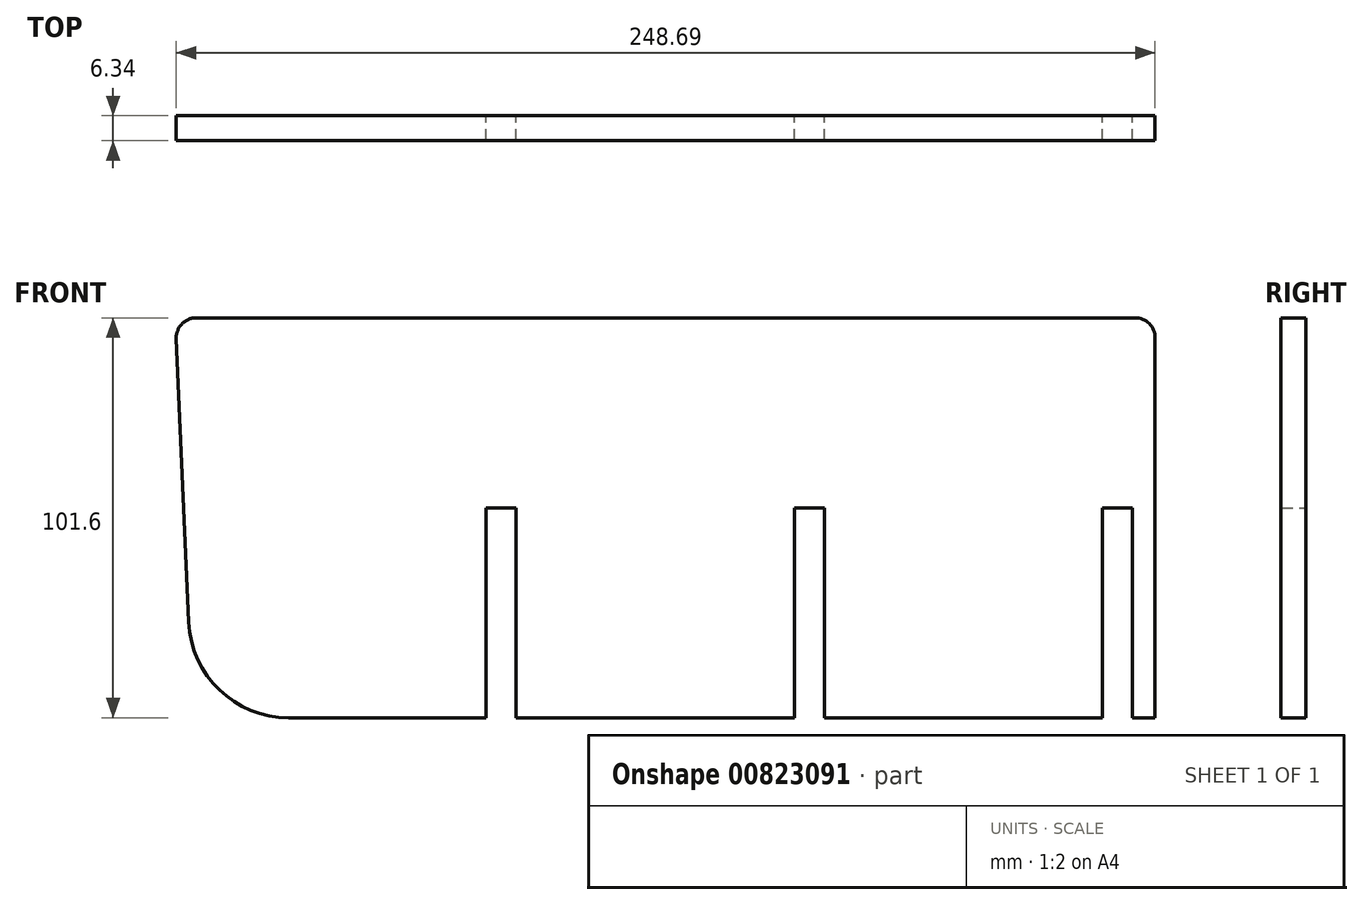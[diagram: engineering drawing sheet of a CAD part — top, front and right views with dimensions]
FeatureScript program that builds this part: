
annotation { "Feature Type Name" : "Feature", "Feature Type Description" : "" }
export const myFeature = defineFeature(function(context is Context, id is Id, definition is map)
    precondition{}
    {
        {
            var Q0;
            Q0=qCreatedBy(makeId("Front.planeOp"),FACE);
            var sketch = newSketch(context, id + "F0", { "sketchPlane" : qUnion([Q0])});
            skLineSegment(sketch, "E0", {"start": v(-126.67, 101.6) * mm, "end": v(-122.24, 0) * mm});
            skLineSegment(sketch, "E1", {"start": v(-122.24, 0) * mm, "end": v(-47.72, 0) * mm});
            skLineSegment(sketch, "E2", {"start": v(122.24, 0) * mm, "end": v(122.24, 101.6) * mm});
            skLineSegment(sketch, "E3", {"start": v(122.24, 101.6) * mm, "end": v(-126.67, 101.6) * mm});
            skLineSegment(sketch, "E4", {"start": v(112.71, 112) * mm, "end": v(112.71, -48.09) * mm, "construction": true});
            skLineSegment(sketch, "E5.top", {"start": v(116.52, 53.34) * mm, "end": v(108.9, 53.34) * mm});
            skLineSegment(sketch, "E5.left", {"start": v(116.52, 0) * mm, "end": v(116.52, 53.34) * mm});
            skLineSegment(sketch, "E5.right", {"start": v(108.9, 0) * mm, "end": v(108.9, 53.34) * mm});
            skLineSegment(sketch, "E6.top", {"start": v(38.2, 53.34) * mm, "end": v(30.59, 53.34) * mm});
            skLineSegment(sketch, "E6.left", {"start": v(38.2, 0) * mm, "end": v(38.2, 53.34) * mm});
            skLineSegment(sketch, "E6.right", {"start": v(30.59, 0) * mm, "end": v(30.59, 53.34) * mm});
            skLineSegment(sketch, "E7", {"start": v(34.4, 109.08) * mm, "end": v(34.4, -45.34) * mm, "construction": true});
            skLineSegment(sketch, "E8.MirrorCS", {"start": v(-47.72, 53.34) * mm, "end": v(-40.1, 53.34) * mm});
            skLineSegment(sketch, "E9.MirrorCS", {"start": v(-47.72, 0) * mm, "end": v(-47.72, 53.34) * mm});
            skLineSegment(sketch, "E10.MirrorCS", {"start": v(-40.1, 0) * mm, "end": v(-40.1, 53.34) * mm});
            skLineSegment(sketch, "E11.trimOffspring", {"start": v(38.2, 0) * mm, "end": v(108.9, 0) * mm});
            skLineSegment(sketch, "E12.trimOffspring", {"start": v(116.52, 0) * mm, "end": v(122.24, 0) * mm});
            skLineSegment(sketch, "E13", {"start": v(-40.1, 0) * mm, "end": v(30.59, 0) * mm});
            skLineSegment(sketch, "E14", {"start": v(-43.91, 119.2) * mm, "end": v(-43.91, -27.8) * mm, "construction": true});
            skPoint(sketch, "E14.startSnap0", {"position": v(-43.91, 53.34) * mm});
            skSolve(sketch);
        }
        {
            var Q0;
            Q0 = qSketchRegion(id + "F0", true);
            extrude(context, id + "F1", {"entities" : qUnion([Q0]), "endBound" : BoundingType.SYMMETRIC, "depth" : 6.35 * mm, "offsetDistance" : 25.4 * mm});
        }
        {
            var Q0;
            Q0=makeQuery(id+"F1.opExtrude","SWEPT_EDGE",EDGE,{"disambiguationData":[OSD([sQuery(id+"F0.wireOp",EDGE,"E0"),sQuery(id+"F0.wireOp",EDGE,"E1")])]});
            fillet(context, id + "F2", {"entities" : qUnion([Q0]), "radius" : 25.4 * mm, "tangentPropagation" : true, "allowEdgeOverflow" : false});
        }
        {
            var Q0;
            Q0=makeQuery(id+"F1.opExtrude","SWEPT_EDGE",EDGE,{"disambiguationData":[OSD([sQuery(id+"F0.wireOp",EDGE,"E0"),sQuery(id+"F0.wireOp",EDGE,"E3")])]});
            var Q1;
            Q1=makeQuery(id+"F1.opExtrude","SWEPT_EDGE",EDGE,{"disambiguationData":[OSD([sQuery(id+"F0.wireOp",EDGE,"E2"),sQuery(id+"F0.wireOp",EDGE,"E3")])]});
            fillet(context, id + "F3", {"entities" : qUnion([Q0, Q1]), "radius" : 5.08 * mm, "tangentPropagation" : true, "allowEdgeOverflow" : false});
        }
    });
